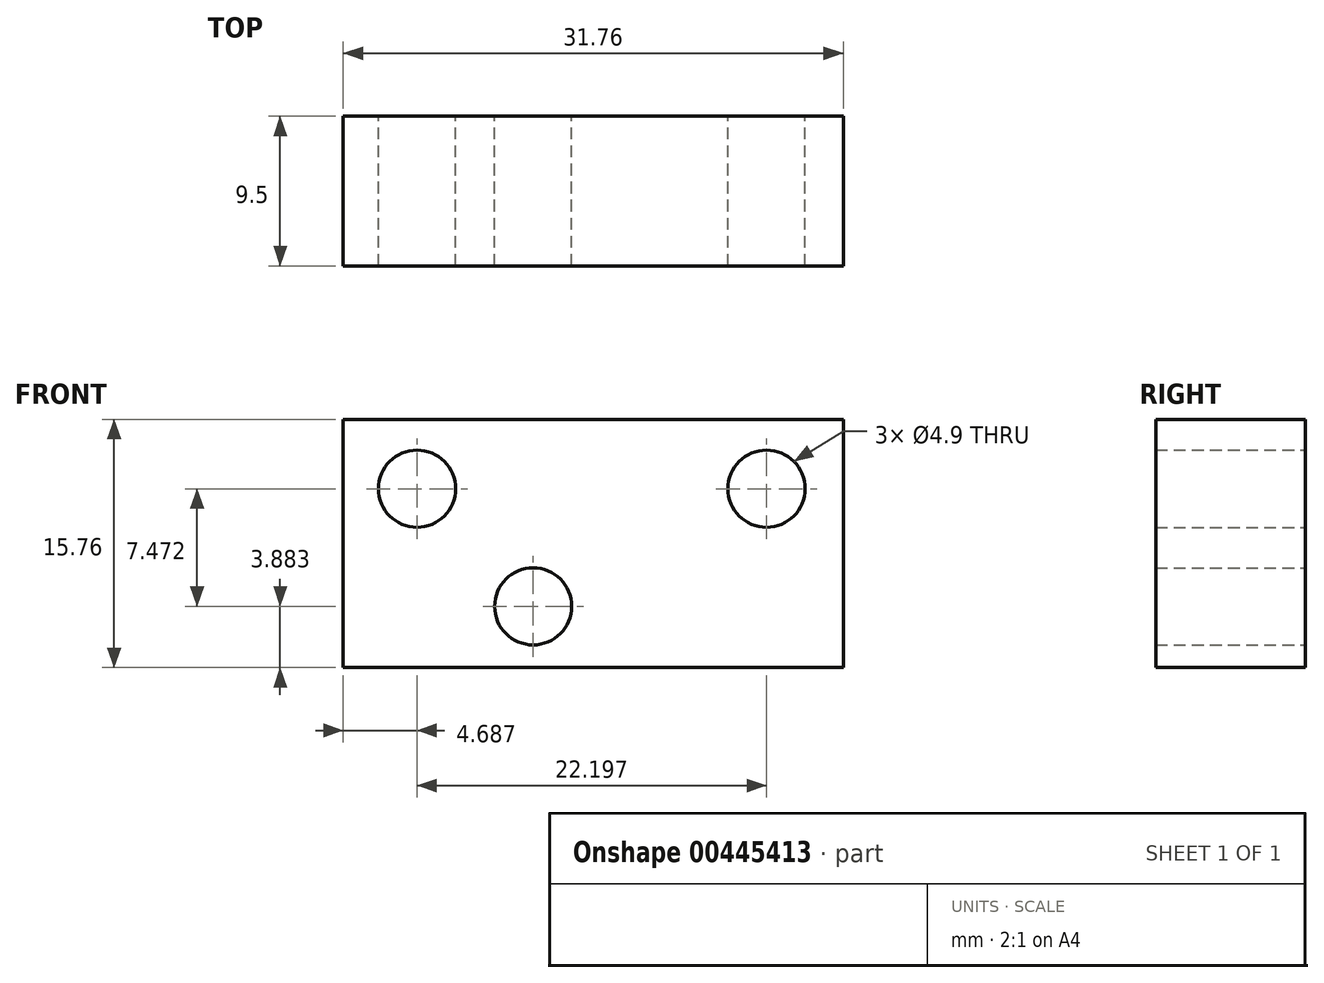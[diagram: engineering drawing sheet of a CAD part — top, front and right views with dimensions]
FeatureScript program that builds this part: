
annotation { "Feature Type Name" : "Feature", "Feature Type Description" : "" }
export const myFeature = defineFeature(function(context is Context, id is Id, definition is map)
    precondition{}
    {
        {
            var Q0;
            Q0=qCreatedBy(makeId("Front.planeOp"),FACE);
            var sketch = newSketch(context, id + "F0", { "sketchPlane" : qUnion([Q0])});
            skLineSegment(sketch, "E0.bottom", {"start": v(15.88, 7.87) * mm, "end": v(-15.88, 7.87) * mm});
            skLineSegment(sketch, "E0.top", {"start": v(15.88, -7.88) * mm, "end": v(-15.88, -7.88) * mm});
            skLineSegment(sketch, "E0.left", {"start": v(15.88, 7.87) * mm, "end": v(15.88, -7.88) * mm});
            skLineSegment(sketch, "E0.right", {"start": v(-15.88, 7.87) * mm, "end": v(-15.88, -7.88) * mm});
            skPoint(sketch, "E0.middle", {"position": v(0, 0) * mm});
            skLineSegment(sketch, "E1", {"start": v(-15.88, 7.87) * mm, "end": v(-15.88, 5.92) * mm});
            skLineSegment(sketch, "E2", {"start": v(-15.88, 5.92) * mm, "end": v(-15.88, 3.47) * mm});
            skLineSegment(sketch, "E3", {"start": v(-15.88, 3.47) * mm, "end": v(15.88, 3.47) * mm});
            skLineSegment(sketch, "E4", {"start": v(-15.88, 3.47) * mm, "end": v(-11.2, 3.47) * mm});
            skCircle(sketch, "E5", {"center": v(-11.2, 3.47) * mm, "radius": 2.45 * mm});
            skCircle(sketch, "E6", {"center": v(-3.82, 3.47) * mm, "radius": 2.45 * mm});
            skCircle(sketch, "E7", {"center": v(3.88, 3.47) * mm, "radius": 2.45 * mm});
            skCircle(sketch, "E8", {"center": v(11, 3.47) * mm, "radius": 2.45 * mm});
            skLineSegment(sketch, "E9", {"start": v(15.88, 3.47) * mm, "end": v(13.41, 3.47) * mm});
            skCircle(sketch, "E10", {"center": v(11, -4) * mm, "radius": 2.45 * mm});
            skLineSegment(sketch, "E11", {"start": v(-15.88, -7.88) * mm, "end": v(-15.88, -4) * mm});
            skLineSegment(sketch, "E12", {"start": v(-15.88, -4) * mm, "end": v(15.88, -4) * mm});
            skCircle(sketch, "E13", {"center": v(3.88, -4) * mm, "radius": 2.45 * mm});
            skCircle(sketch, "E14", {"center": v(-3.82, -4) * mm, "radius": 2.45 * mm});
            skCircle(sketch, "E15", {"center": v(-11.2, -4) * mm, "radius": 2.45 * mm});
            skSolve(sketch);
        }
        {
            var Q0;
            {var subQ0=sQuery(id+"F0.wireOp",EDGE,"E4");var subQ1=sQuery(id+"F0.wireOp",EDGE,"E3");var subQ2=makeQuery(id+"F0.imprint","INTERSECT",VERTEX,{"derivedFrom":[subQ1,subQ0]});Q0=makeQuery(id+"F0.imprint","IMPRINT",FACE,{"disambiguationData":[TD([[makeQuery(id+"F0.imprint","IMPRINT",EDGE,{"disambiguationData":[TD([[subQ2,-1.0]])],"derivedFrom":subQ1}),1.0]])]});}
            var Q1;
            {var subQ0=sQuery(id+"F0.wireOp",EDGE,"E4");var subQ1=sQuery(id+"F0.wireOp",EDGE,"E3");var subQ2=makeQuery(id+"F0.imprint","INTERSECT",VERTEX,{"derivedFrom":[subQ1,subQ0]});Q1=makeQuery(id+"F0.imprint","IMPRINT",FACE,{"disambiguationData":[TD([[makeQuery(id+"F0.imprint","IMPRINT",EDGE,{"disambiguationData":[TD([[subQ2,-1.0]])],"derivedFrom":subQ1}),-1.0]])]});}
            var Q2;
            {var subQ0=sQuery(id+"F0.wireOp",EDGE,"E6");var subQ1=sQuery(id+"F0.wireOp",EDGE,"E3");var subQ2=makeQuery(id+"F0.imprint","INTERSECT",VERTEX,{"disambiguationData":[OD(0.0)],"derivedFrom":[subQ1,subQ0]});Q2=makeQuery(id+"F0.imprint","IMPRINT",FACE,{"disambiguationData":[TD([[makeQuery(id+"F0.imprint","IMPRINT",EDGE,{"disambiguationData":[TD([[subQ2,-1.0]])],"derivedFrom":subQ1}),1.0]])]});}
            var Q3;
            {var subQ0=sQuery(id+"F0.wireOp",EDGE,"E6");var subQ1=sQuery(id+"F0.wireOp",EDGE,"E3");var subQ2=makeQuery(id+"F0.imprint","INTERSECT",VERTEX,{"disambiguationData":[OD(0.0)],"derivedFrom":[subQ1,subQ0]});Q3=makeQuery(id+"F0.imprint","IMPRINT",FACE,{"disambiguationData":[TD([[makeQuery(id+"F0.imprint","IMPRINT",EDGE,{"disambiguationData":[TD([[subQ2,-1.0]])],"derivedFrom":subQ1}),-1.0]])]});}
            var Q4;
            {var subQ0=sQuery(id+"F0.wireOp",EDGE,"E7");var subQ1=sQuery(id+"F0.wireOp",EDGE,"E3");var subQ2=makeQuery(id+"F0.imprint","INTERSECT",VERTEX,{"disambiguationData":[OD(0.0)],"derivedFrom":[subQ1,subQ0]});Q4=makeQuery(id+"F0.imprint","IMPRINT",FACE,{"disambiguationData":[TD([[makeQuery(id+"F0.imprint","IMPRINT",EDGE,{"disambiguationData":[TD([[subQ2,-1.0]])],"derivedFrom":subQ1}),1.0]])]});}
            var Q5;
            {var subQ0=sQuery(id+"F0.wireOp",EDGE,"E7");var subQ1=sQuery(id+"F0.wireOp",EDGE,"E3");var subQ2=makeQuery(id+"F0.imprint","INTERSECT",VERTEX,{"disambiguationData":[OD(0.0)],"derivedFrom":[subQ1,subQ0]});Q5=makeQuery(id+"F0.imprint","IMPRINT",FACE,{"disambiguationData":[TD([[makeQuery(id+"F0.imprint","IMPRINT",EDGE,{"disambiguationData":[TD([[subQ2,-1.0]])],"derivedFrom":subQ1}),-1.0]])]});}
            var Q6;
            {var subQ0=sQuery(id+"F0.wireOp",EDGE,"E9");var subQ1=sQuery(id+"F0.wireOp",EDGE,"E3");var subQ2=makeQuery(id+"F0.imprint","INTERSECT",VERTEX,{"derivedFrom":[subQ1,subQ0]});Q6=makeQuery(id+"F0.imprint","IMPRINT",FACE,{"disambiguationData":[TD([[makeQuery(id+"F0.imprint","IMPRINT",EDGE,{"disambiguationData":[TD([[subQ2,1.0]])],"derivedFrom":subQ1}),1.0]])]});}
            var Q7;
            {var subQ0=sQuery(id+"F0.wireOp",EDGE,"E9");var subQ1=sQuery(id+"F0.wireOp",EDGE,"E3");var subQ2=makeQuery(id+"F0.imprint","INTERSECT",VERTEX,{"derivedFrom":[subQ1,subQ0]});Q7=makeQuery(id+"F0.imprint","IMPRINT",FACE,{"disambiguationData":[TD([[makeQuery(id+"F0.imprint","IMPRINT",EDGE,{"disambiguationData":[TD([[subQ2,1.0]])],"derivedFrom":subQ1}),-1.0]])]});}
            var Q8;
            {var subQ0=sQuery(id+"F0.wireOp",EDGE,"E12");var subQ1=sQuery(id+"F0.wireOp",EDGE,"E10");var subQ2=makeQuery(id+"F0.imprint","INTERSECT",VERTEX,{"disambiguationData":[OD(0.0)],"derivedFrom":[subQ1,subQ0]});Q8=makeQuery(id+"F0.imprint","IMPRINT",FACE,{"disambiguationData":[TD([[makeQuery(id+"F0.imprint","IMPRINT",EDGE,{"disambiguationData":[TD([[subQ2,1.0]])],"derivedFrom":subQ1}),1.0]])]});}
            var Q9;
            {var subQ0=sQuery(id+"F0.wireOp",EDGE,"E12");var subQ1=sQuery(id+"F0.wireOp",EDGE,"E10");var subQ2=makeQuery(id+"F0.imprint","INTERSECT",VERTEX,{"disambiguationData":[OD(0.0)],"derivedFrom":[subQ1,subQ0]});Q9=makeQuery(id+"F0.imprint","IMPRINT",FACE,{"disambiguationData":[TD([[makeQuery(id+"F0.imprint","IMPRINT",EDGE,{"disambiguationData":[TD([[subQ2,-1.0]])],"derivedFrom":subQ1}),1.0]])]});}
            var Q10;
            {var subQ0=sQuery(id+"F0.wireOp",EDGE,"E13");var subQ1=sQuery(id+"F0.wireOp",EDGE,"E12");var subQ2=makeQuery(id+"F0.imprint","INTERSECT",VERTEX,{"disambiguationData":[OD(0.0)],"derivedFrom":[subQ1,subQ0]});Q10=makeQuery(id+"F0.imprint","IMPRINT",FACE,{"disambiguationData":[TD([[makeQuery(id+"F0.imprint","IMPRINT",EDGE,{"disambiguationData":[TD([[subQ2,-1.0]])],"derivedFrom":subQ1}),1.0]])]});}
            var Q11;
            {var subQ0=sQuery(id+"F0.wireOp",EDGE,"E13");var subQ1=sQuery(id+"F0.wireOp",EDGE,"E12");var subQ2=makeQuery(id+"F0.imprint","INTERSECT",VERTEX,{"disambiguationData":[OD(0.0)],"derivedFrom":[subQ1,subQ0]});Q11=makeQuery(id+"F0.imprint","IMPRINT",FACE,{"disambiguationData":[TD([[makeQuery(id+"F0.imprint","IMPRINT",EDGE,{"disambiguationData":[TD([[subQ2,-1.0]])],"derivedFrom":subQ1}),-1.0]])]});}
            var Q12;
            {var subQ0=sQuery(id+"F0.wireOp",EDGE,"E14");var subQ1=sQuery(id+"F0.wireOp",EDGE,"E12");var subQ2=makeQuery(id+"F0.imprint","INTERSECT",VERTEX,{"disambiguationData":[OD(0.0)],"derivedFrom":[subQ1,subQ0]});Q12=makeQuery(id+"F0.imprint","IMPRINT",FACE,{"disambiguationData":[TD([[makeQuery(id+"F0.imprint","IMPRINT",EDGE,{"disambiguationData":[TD([[subQ2,-1.0]])],"derivedFrom":subQ1}),1.0]])]});}
            var Q13;
            {var subQ0=sQuery(id+"F0.wireOp",EDGE,"E14");var subQ1=sQuery(id+"F0.wireOp",EDGE,"E12");var subQ2=makeQuery(id+"F0.imprint","INTERSECT",VERTEX,{"disambiguationData":[OD(0.0)],"derivedFrom":[subQ1,subQ0]});Q13=makeQuery(id+"F0.imprint","IMPRINT",FACE,{"disambiguationData":[TD([[makeQuery(id+"F0.imprint","IMPRINT",EDGE,{"disambiguationData":[TD([[subQ2,-1.0]])],"derivedFrom":subQ1}),-1.0]])]});}
            var Q14;
            {var subQ0=sQuery(id+"F0.wireOp",EDGE,"E15");var subQ1=sQuery(id+"F0.wireOp",EDGE,"E12");var subQ2=makeQuery(id+"F0.imprint","INTERSECT",VERTEX,{"disambiguationData":[OD(0.0)],"derivedFrom":[subQ1,subQ0]});Q14=makeQuery(id+"F0.imprint","IMPRINT",FACE,{"disambiguationData":[TD([[makeQuery(id+"F0.imprint","IMPRINT",EDGE,{"disambiguationData":[TD([[subQ2,-1.0]])],"derivedFrom":subQ1}),1.0]])]});}
            var Q15;
            {var subQ0=sQuery(id+"F0.wireOp",EDGE,"E15");var subQ1=sQuery(id+"F0.wireOp",EDGE,"E12");var subQ2=makeQuery(id+"F0.imprint","INTERSECT",VERTEX,{"disambiguationData":[OD(0.0)],"derivedFrom":[subQ1,subQ0]});Q15=makeQuery(id+"F0.imprint","IMPRINT",FACE,{"disambiguationData":[TD([[makeQuery(id+"F0.imprint","IMPRINT",EDGE,{"disambiguationData":[TD([[subQ2,-1.0]])],"derivedFrom":subQ1}),-1.0]])]});}
            extrude(context, id + "F1", {"entities" : qUnion([Q0, Q1, Q2, Q3, Q4, Q5, Q6, Q7, Q8, Q9, Q10, Q11, Q12, Q13, Q14, Q15]), "depth" : 9.5 * mm});
        }
    });
